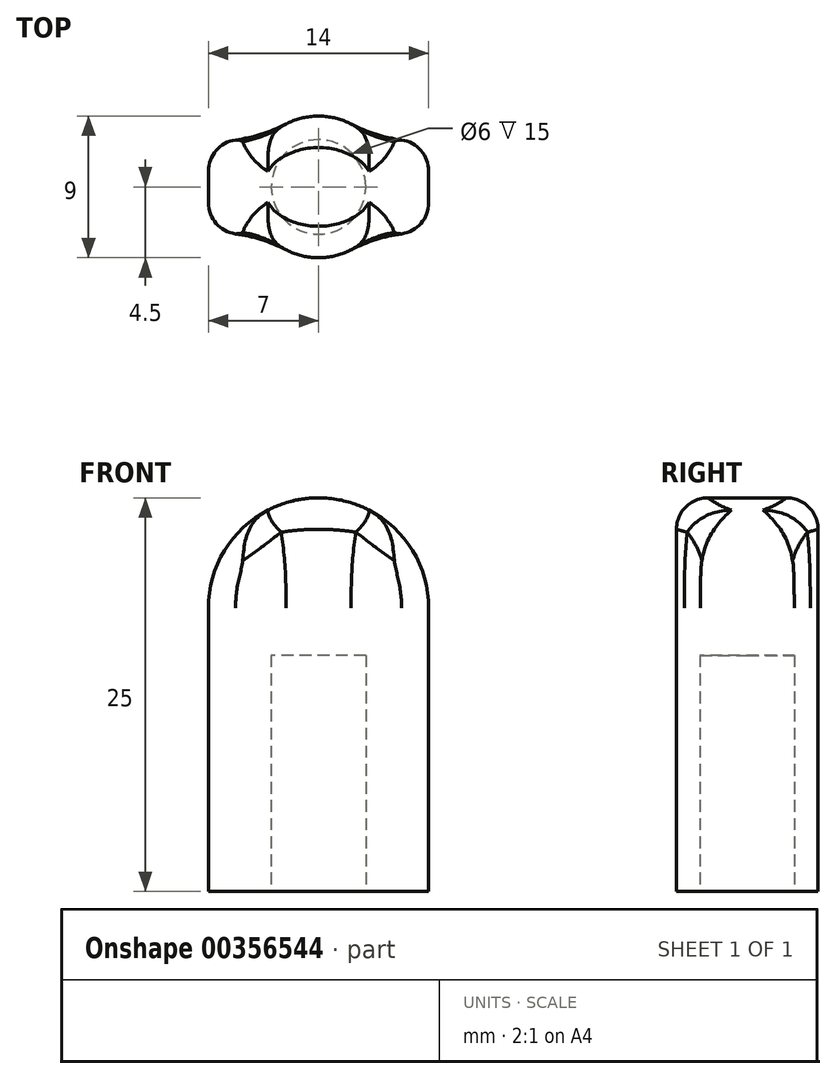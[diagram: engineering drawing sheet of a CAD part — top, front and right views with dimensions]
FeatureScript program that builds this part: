
annotation { "Feature Type Name" : "Feature", "Feature Type Description" : "" }
export const myFeature = defineFeature(function(context is Context, id is Id, definition is map)
    precondition{}
    {
        {
            var Q0;
            Q0=qCreatedBy(makeId("Top.planeOp"),FACE);
            var sketch = newSketch(context, id + "F0", { "sketchPlane" : qUnion([Q0])});
            skCircle(sketch, "E0", {"center": v(0, 0) * mm, "radius": 3 * mm});
            skCircle(sketch, "E1", {"center": v(0, 0) * mm, "radius": 4.5 * mm});
            skLineSegment(sketch, "E2.bottom", {"start": v(7, 3) * mm, "end": v(-7, 3) * mm});
            skLineSegment(sketch, "E2.top", {"start": v(7, -3) * mm, "end": v(-7, -3) * mm});
            skLineSegment(sketch, "E2.left", {"start": v(7, 3) * mm, "end": v(7, -3) * mm});
            skLineSegment(sketch, "E2.right", {"start": v(-7, 3) * mm, "end": v(-7, -3) * mm});
            skSolve(sketch);
        }
        {
            var Q0;
            Q0 = qSketchRegion(id + "F0", true);
            extrude(context, id + "F1", {"entities" : qUnion([Q0]), "depth" : 15 * mm});
        }
        {
            var Q0;
            Q0=makeQuery(id+"F1.opExtrude","CAP_FACE",FACE,{"disambiguationData":[OSD([sQuery(id+"F0.wireOp",EDGE,"E0"),sQuery(id+"F0.wireOp",EDGE,"E1"),sQuery(id+"F0.wireOp",EDGE,"E2.bottom"),sQuery(id+"F0.wireOp",EDGE,"E2.top"),sQuery(id+"F0.wireOp",EDGE,"E2.left"),sQuery(id+"F0.wireOp",EDGE,"E2.right")])],"isStart":false});
            var sketch = newSketch(context, id + "F2", { "sketchPlane" : qUnion([Q0])});
            skCircle(sketch, "E3", {"center": v(0, 0) * mm, "radius": 4.5 * mm});
            skLineSegment(sketch, "E4.bottom", {"start": v(7, 3) * mm, "end": v(-7, 3) * mm});
            skLineSegment(sketch, "E4.top", {"start": v(7, -3) * mm, "end": v(-7, -3) * mm});
            skLineSegment(sketch, "E4.left", {"start": v(7, 3) * mm, "end": v(7, -3) * mm});
            skLineSegment(sketch, "E4.right", {"start": v(-7, 3) * mm, "end": v(-7, -3) * mm});
            skSolve(sketch);
        }
        {
            var Q0;
            Q0 = qSketchRegion(id + "F2", true);
            extrude(context, id + "F3", {"entities" : qUnion([Q0]), "operationType" : NewBodyOperationType.ADD, "depth" : 10 * mm});
        }
        {
            var Q0;
            Q0=makeQuery(id+"F3.opExtrude","CAP_EDGE",EDGE,{"disambiguationData":[OSD([sQuery(id+"F2.wireOp",EDGE,"E4.right")])],"isStart":false});
            var Q1;
            Q1=makeQuery(id+"F3.opExtrude","CAP_EDGE",EDGE,{"disambiguationData":[OSD([sQuery(id+"F2.wireOp",EDGE,"E4.left")])],"isStart":false});
            fillet(context, id + "F4", {"entities" : qUnion([Q0, Q1]), "radius" : 7 * mm, "tangentPropagation" : true, "allowEdgeOverflow" : false});
        }
        {
            var Q0;
            Q0=makeQuery(id+"F3.boolean.opBoolean","MERGE",EDGE,{"derivedFrom":[makeQuery(id+"F1.opExtrude","SWEPT_EDGE",EDGE,{"disambiguationData":[OSD([sQuery(id+"F0.wireOp",EDGE,"E2.bottom"),sQuery(id+"F0.wireOp",EDGE,"E2.right")])]}),makeQuery(id+"F3.opExtrude","SWEPT_EDGE",EDGE,{"disambiguationData":[OSD([sQuery(id+"F2.wireOp",EDGE,"E4.bottom"),sQuery(id+"F2.wireOp",EDGE,"E4.right")])]})]});
            var Q1;
            Q1=makeQuery(id+"F3.boolean.opBoolean","MERGE",EDGE,{"derivedFrom":[makeQuery(id+"F1.opExtrude","SWEPT_EDGE",EDGE,{"disambiguationData":[OSD([sQuery(id+"F0.wireOp",EDGE,"E2.top"),sQuery(id+"F0.wireOp",EDGE,"E2.right")])]}),makeQuery(id+"F3.opExtrude","SWEPT_EDGE",EDGE,{"disambiguationData":[OSD([sQuery(id+"F2.wireOp",EDGE,"E4.top"),sQuery(id+"F2.wireOp",EDGE,"E4.right")])]})]});
            var Q2;
            Q2=makeQuery(id+"F3.boolean.opBoolean","MERGE",EDGE,{"derivedFrom":[makeQuery(id+"F1.opExtrude","SWEPT_EDGE",EDGE,{"disambiguationData":[OSD([sQuery(id+"F0.wireOp",EDGE,"E2.top"),sQuery(id+"F0.wireOp",EDGE,"E2.left")])]}),makeQuery(id+"F3.opExtrude","SWEPT_EDGE",EDGE,{"disambiguationData":[OSD([sQuery(id+"F2.wireOp",EDGE,"E4.top"),sQuery(id+"F2.wireOp",EDGE,"E4.left")])]})]});
            var Q3;
            Q3=makeQuery(id+"F3.boolean.opBoolean","MERGE",EDGE,{"derivedFrom":[makeQuery(id+"F1.opExtrude","SWEPT_EDGE",EDGE,{"disambiguationData":[OSD([sQuery(id+"F0.wireOp",EDGE,"E2.bottom"),sQuery(id+"F0.wireOp",EDGE,"E2.left")])]}),makeQuery(id+"F3.opExtrude","SWEPT_EDGE",EDGE,{"disambiguationData":[OSD([sQuery(id+"F2.wireOp",EDGE,"E4.bottom"),sQuery(id+"F2.wireOp",EDGE,"E4.left")])]})]});
            var Q4;
            {var subQ0=sQuery(id+"F2.wireOp",EDGE,"E4.top");var subQ1=sQuery(id+"F2.wireOp",EDGE,"E3");var subQ2=sQuery(id+"F0.wireOp",EDGE,"E2.top");var subQ3=sQuery(id+"F0.wireOp",EDGE,"E1");Q4=makeQuery(id+"F4.opFillet","BLEND_EDGE",EDGE,{"blendedFrom":[makeQuery(id+"F3.opExtrude","CAP_EDGE",EDGE,{"disambiguationData":[OSD([sQuery(id+"F2.wireOp",EDGE,"E4.right")])],"isStart":false}),makeQuery(id+"F3.boolean.opBoolean","MERGE",FACE,{"derivedFrom":[makeQuery(id+"F1.opExtrude","SWEPT_FACE",FACE,{"disambiguationData":[OSD([subQ3]),TDD([makeQuery(id+"F0.imprint","IMPRINT",EDGE,{"disambiguationData":[TD([[makeQuery(id+"F0.imprint","INTERSECT",VERTEX,{"disambiguationData":[OD(0.0)],"derivedFrom":[subQ3,subQ2]}),-1.0]])],"derivedFrom":subQ3})])]}),makeQuery(id+"F3.opExtrude","SWEPT_FACE",FACE,{"disambiguationData":[OSD([subQ1]),TDD([makeQuery(id+"F2.imprint","IMPRINT",EDGE,{"disambiguationData":[TD([[makeQuery(id+"F2.imprint","INTERSECT",VERTEX,{"disambiguationData":[OD(0.0)],"derivedFrom":[subQ1,subQ0]}),-1.0]])],"derivedFrom":subQ1})])]})]})],"blendedInto":[makeQuery(id+"F3.boolean.opBoolean","MERGE",FACE,{"derivedFrom":[makeQuery(id+"F1.opExtrude","SWEPT_FACE",FACE,{"disambiguationData":[OSD([subQ3]),TDD([makeQuery(id+"F0.imprint","IMPRINT",EDGE,{"disambiguationData":[TD([[makeQuery(id+"F0.imprint","INTERSECT",VERTEX,{"disambiguationData":[OD(0.0)],"derivedFrom":[subQ3,subQ2]}),-1.0]])],"derivedFrom":subQ3})])]}),makeQuery(id+"F3.opExtrude","SWEPT_FACE",FACE,{"disambiguationData":[OSD([subQ1]),TDD([makeQuery(id+"F2.imprint","IMPRINT",EDGE,{"disambiguationData":[TD([[makeQuery(id+"F2.imprint","INTERSECT",VERTEX,{"disambiguationData":[OD(0.0)],"derivedFrom":[subQ1,subQ0]}),-1.0]])],"derivedFrom":subQ1})])]})]})]});}
            var Q5;
            {var subQ0=sQuery(id+"F2.wireOp",EDGE,"E4.bottom");var subQ1=sQuery(id+"F2.wireOp",EDGE,"E3");var subQ2=sQuery(id+"F0.wireOp",EDGE,"E2.bottom");var subQ3=sQuery(id+"F0.wireOp",EDGE,"E1");Q5=makeQuery(id+"F4.opFillet","BLEND_EDGE",EDGE,{"blendedFrom":[makeQuery(id+"F3.opExtrude","CAP_EDGE",EDGE,{"disambiguationData":[OSD([sQuery(id+"F2.wireOp",EDGE,"E4.right")])],"isStart":false}),makeQuery(id+"F3.boolean.opBoolean","MERGE",FACE,{"derivedFrom":[makeQuery(id+"F1.opExtrude","SWEPT_FACE",FACE,{"disambiguationData":[OSD([subQ3]),TDD([makeQuery(id+"F0.imprint","IMPRINT",EDGE,{"disambiguationData":[TD([[makeQuery(id+"F0.imprint","INTERSECT",VERTEX,{"disambiguationData":[OD(0.0)],"derivedFrom":[subQ3,subQ2]}),1.0]])],"derivedFrom":subQ3})])]}),makeQuery(id+"F3.opExtrude","SWEPT_FACE",FACE,{"disambiguationData":[OSD([subQ1]),TDD([makeQuery(id+"F2.imprint","IMPRINT",EDGE,{"disambiguationData":[TD([[makeQuery(id+"F2.imprint","INTERSECT",VERTEX,{"disambiguationData":[OD(0.0)],"derivedFrom":[subQ1,subQ0]}),1.0]])],"derivedFrom":subQ1})])]})]})],"blendedInto":[makeQuery(id+"F3.boolean.opBoolean","MERGE",FACE,{"derivedFrom":[makeQuery(id+"F1.opExtrude","SWEPT_FACE",FACE,{"disambiguationData":[OSD([subQ3]),TDD([makeQuery(id+"F0.imprint","IMPRINT",EDGE,{"disambiguationData":[TD([[makeQuery(id+"F0.imprint","INTERSECT",VERTEX,{"disambiguationData":[OD(0.0)],"derivedFrom":[subQ3,subQ2]}),1.0]])],"derivedFrom":subQ3})])]}),makeQuery(id+"F3.opExtrude","SWEPT_FACE",FACE,{"disambiguationData":[OSD([subQ1]),TDD([makeQuery(id+"F2.imprint","IMPRINT",EDGE,{"disambiguationData":[TD([[makeQuery(id+"F2.imprint","INTERSECT",VERTEX,{"disambiguationData":[OD(0.0)],"derivedFrom":[subQ1,subQ0]}),1.0]])],"derivedFrom":subQ1})])]})]})]});}
            fillet(context, id + "F5", {"entities" : qUnion([Q0, Q1, Q2, Q3, Q4, Q5]), "radius" : 2 * mm, "tangentPropagation" : true, "allowEdgeOverflow" : false});
        }
        {
            var Q0;
            {var subQ0=sQuery(id+"F2.wireOp",EDGE,"E4.bottom");var subQ1=sQuery(id+"F2.wireOp",EDGE,"E3");var subQ2=sQuery(id+"F0.wireOp",EDGE,"E2.bottom");var subQ3=sQuery(id+"F0.wireOp",EDGE,"E1");Q0=makeQuery(id+"F3.boolean.opBoolean","MERGE",EDGE,{"derivedFrom":[makeQuery(id+"F1.opExtrude","SWEPT_EDGE",EDGE,{"disambiguationData":[OSD([subQ3,subQ2]),TDD([makeQuery(id+"F0.imprint","INTERSECT",VERTEX,{"disambiguationData":[OD(1.0)],"derivedFrom":[subQ3,subQ2]})])]}),makeQuery(id+"F3.opExtrude","SWEPT_EDGE",EDGE,{"disambiguationData":[OSD([subQ1,subQ0]),TDD([makeQuery(id+"F2.imprint","INTERSECT",VERTEX,{"disambiguationData":[OD(1.0)],"derivedFrom":[subQ1,subQ0]})])]})]});}
            var Q1;
            {var subQ0=sQuery(id+"F2.wireOp",EDGE,"E4.bottom");var subQ1=sQuery(id+"F2.wireOp",EDGE,"E3");var subQ2=sQuery(id+"F0.wireOp",EDGE,"E2.bottom");var subQ3=sQuery(id+"F0.wireOp",EDGE,"E1");Q1=makeQuery(id+"F3.boolean.opBoolean","MERGE",EDGE,{"derivedFrom":[makeQuery(id+"F1.opExtrude","SWEPT_EDGE",EDGE,{"disambiguationData":[OSD([subQ3,subQ2]),TDD([makeQuery(id+"F0.imprint","INTERSECT",VERTEX,{"disambiguationData":[OD(0.0)],"derivedFrom":[subQ3,subQ2]})])]}),makeQuery(id+"F3.opExtrude","SWEPT_EDGE",EDGE,{"disambiguationData":[OSD([subQ1,subQ0]),TDD([makeQuery(id+"F2.imprint","INTERSECT",VERTEX,{"disambiguationData":[OD(0.0)],"derivedFrom":[subQ1,subQ0]})])]})]});}
            var Q2;
            {var subQ0=sQuery(id+"F2.wireOp",EDGE,"E4.top");var subQ1=sQuery(id+"F2.wireOp",EDGE,"E3");var subQ2=sQuery(id+"F0.wireOp",EDGE,"E2.top");var subQ3=sQuery(id+"F0.wireOp",EDGE,"E1");Q2=makeQuery(id+"F3.boolean.opBoolean","MERGE",EDGE,{"derivedFrom":[makeQuery(id+"F1.opExtrude","SWEPT_EDGE",EDGE,{"disambiguationData":[OSD([subQ3,subQ2]),TDD([makeQuery(id+"F0.imprint","INTERSECT",VERTEX,{"disambiguationData":[OD(0.0)],"derivedFrom":[subQ3,subQ2]})])]}),makeQuery(id+"F3.opExtrude","SWEPT_EDGE",EDGE,{"disambiguationData":[OSD([subQ1,subQ0]),TDD([makeQuery(id+"F2.imprint","INTERSECT",VERTEX,{"disambiguationData":[OD(0.0)],"derivedFrom":[subQ1,subQ0]})])]})]});}
            var Q3;
            {var subQ0=sQuery(id+"F2.wireOp",EDGE,"E4.top");var subQ1=sQuery(id+"F2.wireOp",EDGE,"E3");var subQ2=sQuery(id+"F0.wireOp",EDGE,"E2.top");var subQ3=sQuery(id+"F0.wireOp",EDGE,"E1");Q3=makeQuery(id+"F3.boolean.opBoolean","MERGE",EDGE,{"derivedFrom":[makeQuery(id+"F1.opExtrude","SWEPT_EDGE",EDGE,{"disambiguationData":[OSD([subQ3,subQ2]),TDD([makeQuery(id+"F0.imprint","INTERSECT",VERTEX,{"disambiguationData":[OD(1.0)],"derivedFrom":[subQ3,subQ2]})])]}),makeQuery(id+"F3.opExtrude","SWEPT_EDGE",EDGE,{"disambiguationData":[OSD([subQ1,subQ0]),TDD([makeQuery(id+"F2.imprint","INTERSECT",VERTEX,{"disambiguationData":[OD(1.0)],"derivedFrom":[subQ1,subQ0]})])]})]});}
            fillet(context, id + "F6", {"entities" : qUnion([Q0, Q1, Q2, Q3]), "radius" : 10 * mm, "tangentPropagation" : true, "allowEdgeOverflow" : false});
        }
    });
